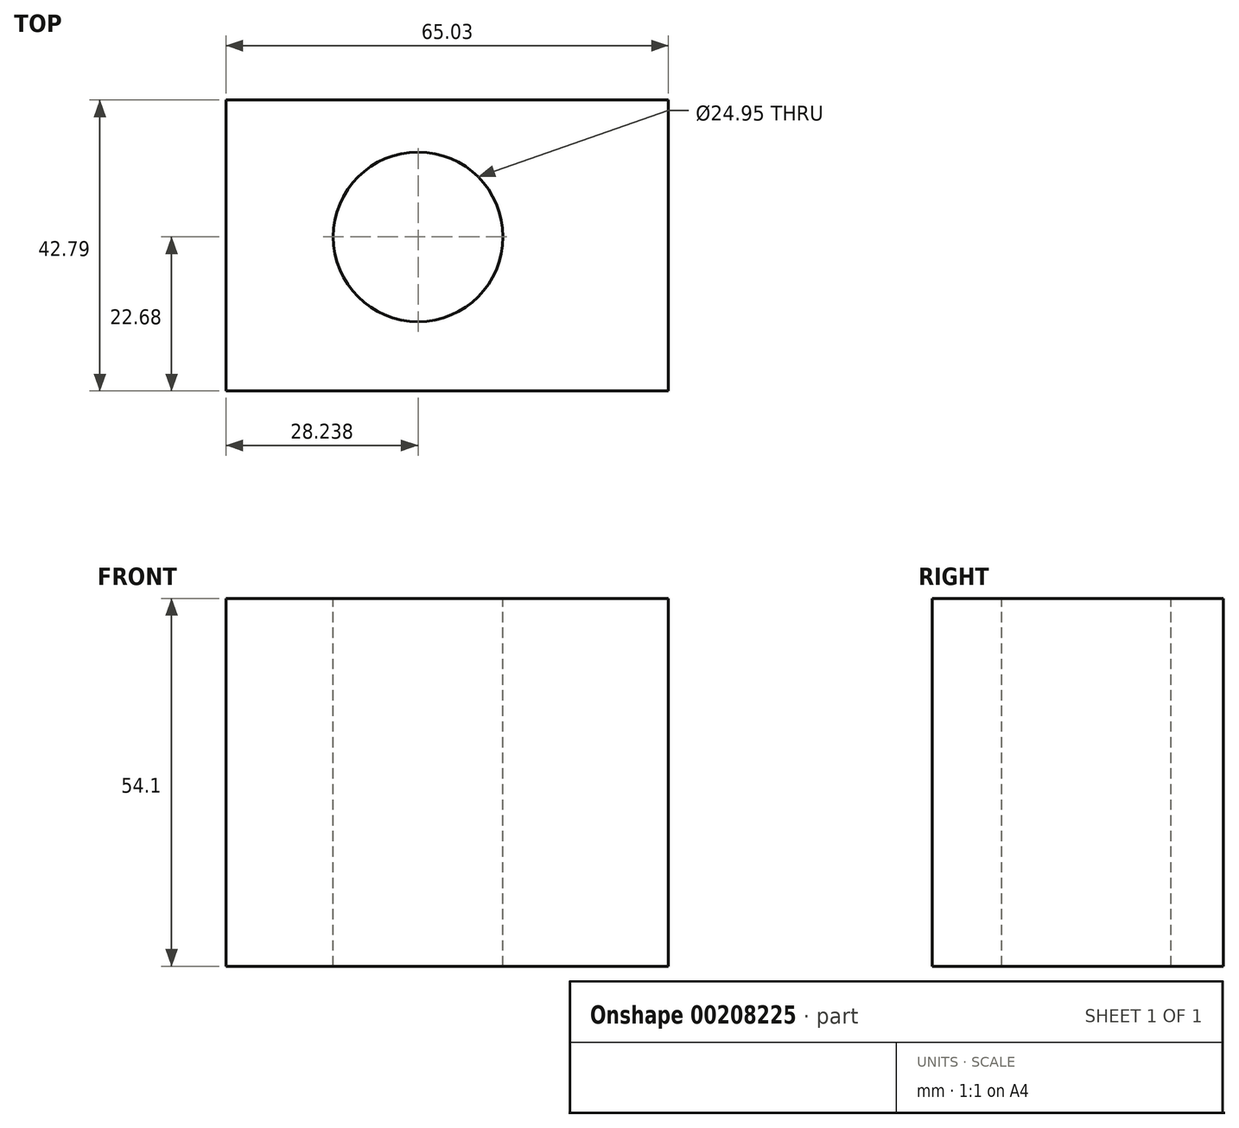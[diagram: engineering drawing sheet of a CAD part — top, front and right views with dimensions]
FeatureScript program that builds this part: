
annotation { "Feature Type Name" : "Feature", "Feature Type Description" : "" }
export const myFeature = defineFeature(function(context is Context, id is Id, definition is map)
    precondition{}
    {
        {
            var Q0;
            Q0=qCreatedBy(makeId("Top.planeOp"),FACE);
            var sketch = newSketch(context, id + "F0", { "sketchPlane" : qUnion([Q0])});
            skLineSegment(sketch, "E0.bottom", {"start": v(-31.1, 20.1) * mm, "end": v(33.94, 20.1) * mm});
            skLineSegment(sketch, "E0.top", {"start": v(-31.1, -22.68) * mm, "end": v(33.94, -22.68) * mm});
            skLineSegment(sketch, "E0.left", {"start": v(-31.1, 20.1) * mm, "end": v(-31.1, -22.68) * mm});
            skLineSegment(sketch, "E0.right", {"start": v(33.94, 20.1) * mm, "end": v(33.94, -22.68) * mm});
            skSolve(sketch);
        }
        {
            var Q0;
            Q0=makeQuery(id+"F0.imprint","IMPRINT",FACE,{"disambiguationData":[TD([[makeQuery(id+"F0.imprint","IMPRINT",EDGE,{"derivedFrom":sQuery(id+"F0.wireOp",EDGE,"E0.bottom")}),-1.0]])]});
            extrude(context, id + "F1", {"entities" : qUnion([Q0]), "oppositeDirection" : true, "depth" : 54.1 * mm});
        }
        {
            var Q0;
            Q0=makeQuery(id+"F1.opExtrude","CAP_FACE",FACE,{"disambiguationData":[OSD([sQuery(id+"F0.wireOp",EDGE,"E0.bottom"),sQuery(id+"F0.wireOp",EDGE,"E0.top"),sQuery(id+"F0.wireOp",EDGE,"E0.left"),sQuery(id+"F0.wireOp",EDGE,"E0.right")])],"isStart":true});
            var sketch = newSketch(context, id + "F2", { "sketchPlane" : qUnion([Q0])});
            skCircle(sketch, "E1", {"center": v(-2.85, 0) * mm, "radius": 12.47 * mm});
            skSolve(sketch);
        }
        {
            var Q0;
            Q0=makeQuery(id+"F2.imprint","IMPRINT",FACE,{"disambiguationData":[TD([[makeQuery(id+"F2.imprint","IMPRINT",EDGE,{"derivedFrom":sQuery(id+"F2.wireOp",EDGE,"E1")}),1.0]])]});
            extrude(context, id + "F3", {"entities" : qUnion([Q0]), "operationType" : NewBodyOperationType.REMOVE, "oppositeDirection" : true, "depth" : 62.74 * mm});
        }
    });
